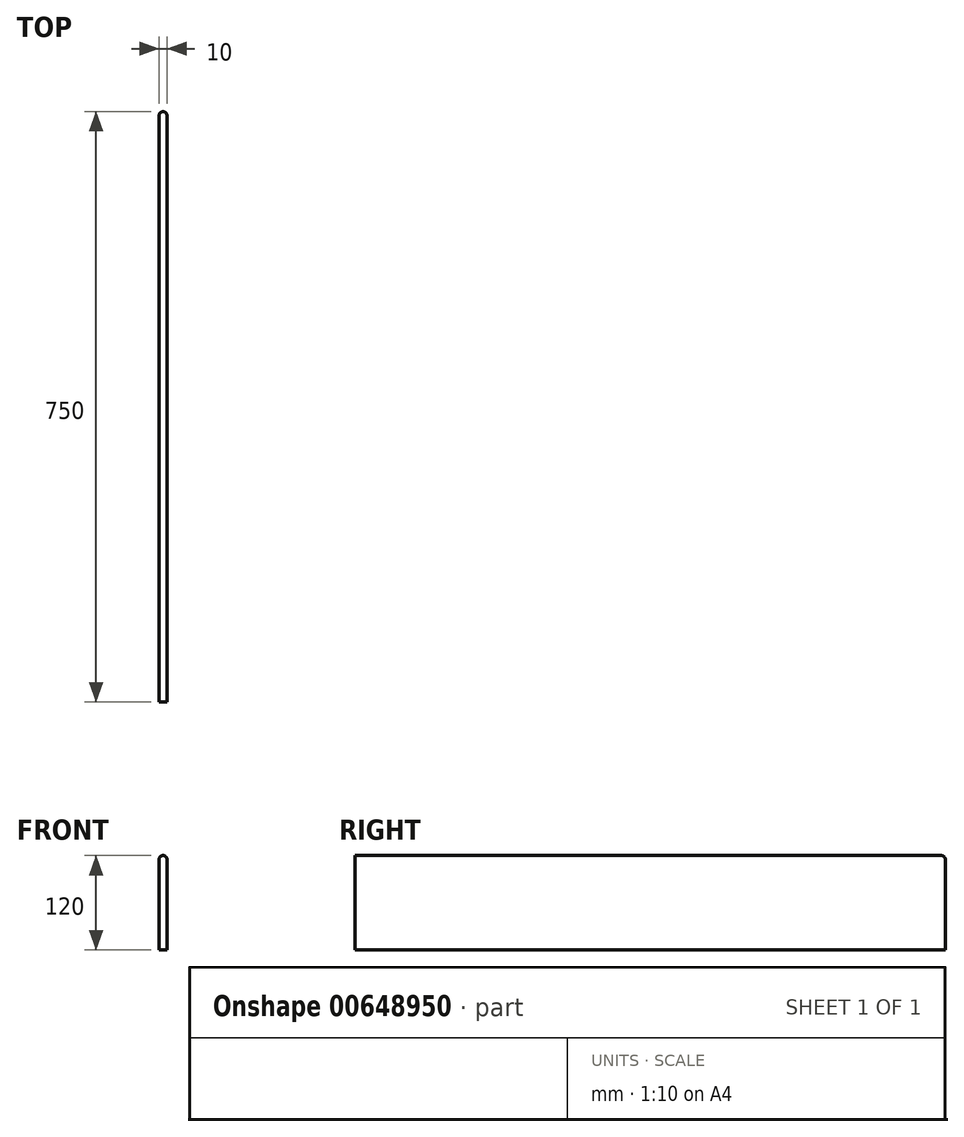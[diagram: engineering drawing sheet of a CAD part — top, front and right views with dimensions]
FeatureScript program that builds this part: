
annotation { "Feature Type Name" : "Feature", "Feature Type Description" : "" }
export const myFeature = defineFeature(function(context is Context, id is Id, definition is map)
    precondition{}
    {
        {
            var Q0;
            Q0=qCreatedBy(makeId("Right.planeOp"),FACE);
            var sketch = newSketch(context, id + "F0", { "sketchPlane" : qUnion([Q0])});
            skLineSegment(sketch, "E0.bottom", {"start": v(375, -60) * mm, "end": v(-375, -60) * mm});
            skLineSegment(sketch, "E0.top", {"start": v(375, 60) * mm, "end": v(-375, 60) * mm});
            skLineSegment(sketch, "E0.left", {"start": v(375, -60) * mm, "end": v(375, 60) * mm});
            skLineSegment(sketch, "E0.right", {"start": v(-375, -60) * mm, "end": v(-375, 60) * mm});
            skPoint(sketch, "E0.middle", {"position": v(0, 0) * mm});
            skSolve(sketch);
        }
        {
            var Q0;
            Q0=qSketchRegion(id+"F0",true);
            extrude(context, id + "F1", {"entities" : qUnion([Q0]), "depth" : 10 * mm, "offsetDistance" : 25 * mm});
        }
        {
            var Q0;
            Q0=makeQuery(id+"F1.opExtrude","CAP_EDGE",EDGE,{"disambiguationData":[OSD([sQuery(id+"F0.wireOp",EDGE,"E0.left")])],"isStart":false});
            var Q1;
            Q1=makeQuery(id+"F1.opExtrude","SWEPT_EDGE",EDGE,{"disambiguationData":[OSD([sQuery(id+"F0.wireOp",EDGE,"E0.top"),sQuery(id+"F0.wireOp",EDGE,"E0.left")])]});
            var Q2;
            Q2=makeQuery(id+"F1.opExtrude","CAP_EDGE",EDGE,{"disambiguationData":[OSD([sQuery(id+"F0.wireOp",EDGE,"E0.left")])],"isStart":true});
            var Q3;
            Q3=makeQuery(id+"F1.opExtrude","CAP_EDGE",EDGE,{"disambiguationData":[OSD([sQuery(id+"F0.wireOp",EDGE,"E0.top")])],"isStart":true});
            var Q4;
            Q4=makeQuery(id+"F1.opExtrude","CAP_EDGE",EDGE,{"disambiguationData":[OSD([sQuery(id+"F0.wireOp",EDGE,"E0.top")])],"isStart":false});
            fillet(context, id + "F2", {"entities" : qUnion([Q0, Q1, Q2, Q3, Q4]), "radius" : 5 * mm, "tangentPropagation" : true, "allowEdgeOverflow" : false});
        }
    });
